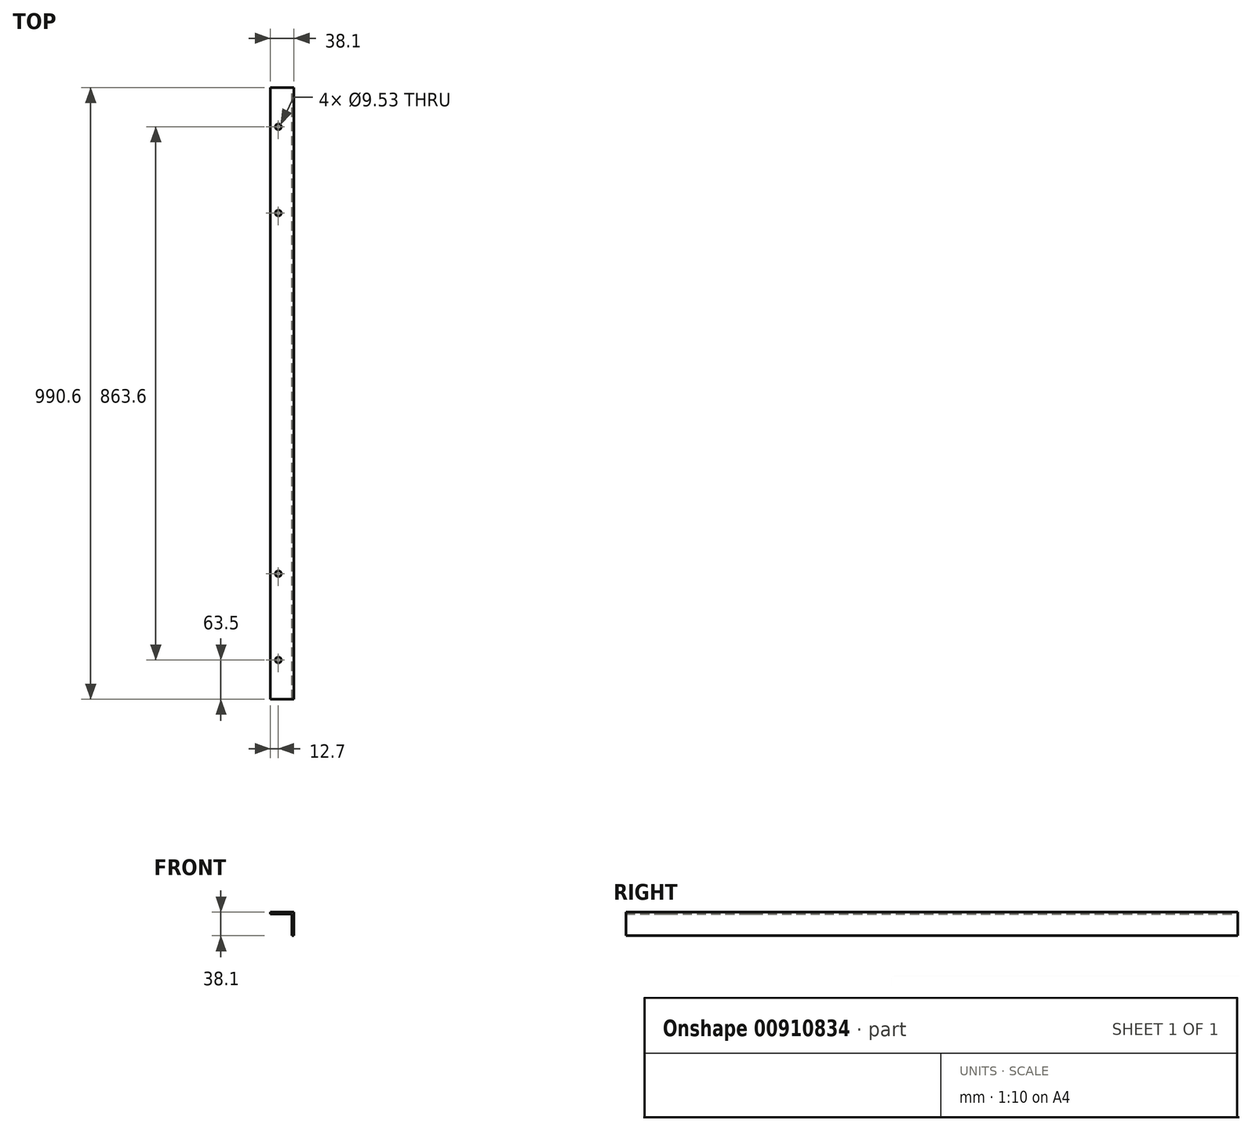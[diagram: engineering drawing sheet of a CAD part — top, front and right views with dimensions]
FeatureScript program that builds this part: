
annotation { "Feature Type Name" : "Feature", "Feature Type Description" : "" }
export const myFeature = defineFeature(function(context is Context, id is Id, definition is map)
    precondition{}
    {
        {
            var Q0;
            Q0=qCreatedBy(makeId("Front.planeOp"),FACE);
            var sketch = newSketch(context, id + "F0", { "sketchPlane" : qUnion([Q0])});
            skLineSegment(sketch, "E0", {"start": v(0, 0) * mm, "end": v(38.1, 0) * mm});
            skLineSegment(sketch, "E1", {"start": v(38.1, 0) * mm, "end": v(38.1, -38.1) * mm});
            skLineSegment(sketch, "E2.0", {"start": v(34.92, -3.18) * mm, "end": v(34.92, -38.1) * mm});
            skLineSegment(sketch, "E2.1", {"start": v(0, -3.18) * mm, "end": v(34.92, -3.18) * mm});
            skLineSegment(sketch, "E3", {"start": v(0, 0) * mm, "end": v(0, -3.18) * mm});
            skLineSegment(sketch, "E4", {"start": v(38.1, -38.1) * mm, "end": v(34.92, -38.1) * mm});
            skSolve(sketch);
        }
        {
            var Q0;
            Q0 = qSketchRegion(id + "F0", true);
            extrude(context, id + "F1", {"entities" : qUnion([Q0]), "depth" : 990.6 * mm, "offsetDistance" : 25.4 * mm});
        }
        {
            var Q0;
            Q0=makeQuery(id+"F1.opExtrude","SWEPT_FACE",FACE,{"disambiguationData":[OSD([sQuery(id+"F0.wireOp",EDGE,"E0")])]});
            var sketch = newSketch(context, id + "F2", { "sketchPlane" : qUnion([Q0])});
            skCircle(sketch, "E5", {"center": v(12.7, -927.1) * mm, "radius": 4.76 * mm});
            skCircle(sketch, "E6", {"center": v(12.7, -787.4) * mm, "radius": 4.76 * mm});
            skCircle(sketch, "E7", {"center": v(12.7, -203.2) * mm, "radius": 4.76 * mm});
            skCircle(sketch, "E8", {"center": v(12.7, -63.5) * mm, "radius": 4.76 * mm});
            skSolve(sketch);
        }
        {
            var Q0;
            Q0 = qSketchRegion(id + "F2", true);
            extrude(context, id + "F3", {"entities" : qUnion([Q0]), "operationType" : NewBodyOperationType.REMOVE, "endBound" : BoundingType.THROUGH_ALL, "oppositeDirection" : true, "depth" : 25.4 * mm, "offsetDistance" : 25.4 * mm});
        }
    });
